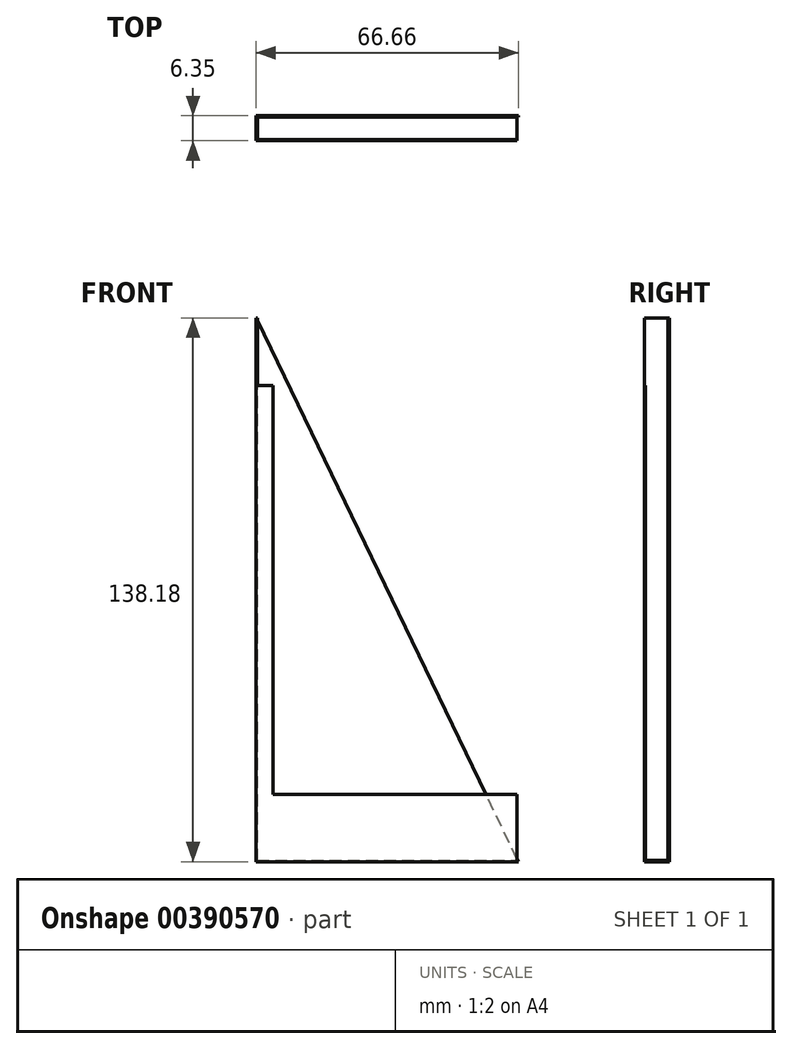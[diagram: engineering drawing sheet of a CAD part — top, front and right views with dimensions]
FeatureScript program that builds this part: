
annotation { "Feature Type Name" : "Feature", "Feature Type Description" : "" }
export const myFeature = defineFeature(function(context is Context, id is Id, definition is map)
    precondition{}
    {
        {
            var Q0;
            Q0=qCreatedBy(makeId("Front.planeOp"),FACE);
            var sketch = newSketch(context, id + "F0", { "sketchPlane" : qUnion([Q0])});
            skLineSegment(sketch, "E0.bottom", {"start": v(-33.53, -69.09) * mm, "end": v(33.13, -69.09) * mm});
            skLineSegment(sketch, "E0.left", {"start": v(-33.53, -69.09) * mm, "end": v(-33.53, 69.09) * mm});
            skLineSegment(sketch, "E1", {"start": v(-29.22, -51.97) * mm, "end": v(-29.22, 60.15) * mm});
            skLineSegment(sketch, "E2", {"start": v(-29.22, -51.97) * mm, "end": v(33.13, -51.97) * mm});
            skLineSegment(sketch, "E3", {"start": v(-29.22, 60.15) * mm, "end": v(-29.22, 69.09) * mm});
            skLineSegment(sketch, "E4", {"start": v(-29.22, 69.09) * mm, "end": v(-33.53, 69.09) * mm});
            skLineSegment(sketch, "E5", {"start": v(33.13, -51.97) * mm, "end": v(33.13, -69.09) * mm});
            skSolve(sketch);
        }
        {
            var Q0;
            Q0 = qSketchRegion(id + "F0", true);
            extrude(context, id + "F1", {"entities" : qUnion([Q0]), "depth" : 6.35 * mm});
        }
        {
            var Q0;
            Q0=qCreatedBy(makeId("Right.planeOp"),FACE);
            var sketch = newSketch(context, id + "F2", { "sketchPlane" : qUnion([Q0])});
            skLineSegment(sketch, "E6.bottom", {"start": v(-6.03, 51.97) * mm, "end": v(-0.32, 51.97) * mm});
            skLineSegment(sketch, "E6.top", {"start": v(-6.03, 68.77) * mm, "end": v(-0.32, 68.77) * mm});
            skLineSegment(sketch, "E6.left", {"start": v(-6.03, 51.97) * mm, "end": v(-6.03, 68.77) * mm});
            skLineSegment(sketch, "E6.right", {"start": v(-0.32, 51.97) * mm, "end": v(-0.32, 68.77) * mm});
            skLineSegment(sketch, "E7.bottom", {"start": v(-0.32, -51.97) * mm, "end": v(-6.03, -51.97) * mm});
            skLineSegment(sketch, "E7.top", {"start": v(-6.03, -68.77) * mm, "end": v(-0.32, -68.77) * mm});
            skLineSegment(sketch, "E7.left", {"start": v(-6.03, -51.97) * mm, "end": v(-6.03, -68.77) * mm});
            skLineSegment(sketch, "E7.right", {"start": v(-0.32, -51.97) * mm, "end": v(-0.32, -68.77) * mm});
            skSolve(sketch);
        }
        {
            var Q0;
            Q0 = qSketchRegion(id + "F2", true);
            extrude(context, id + "F3", {"entities" : qUnion([Q0]), "operationType" : NewBodyOperationType.REMOVE, "endBound" : BoundingType.SYMMETRIC, "oppositeDirection" : true, "depth" : 66.02 * mm});
        }
        {
            var Q0;
            Q0=qCreatedBy(makeId("Top.planeOp"),FACE);
            var sketch = newSketch(context, id + "F4", { "sketchPlane" : qUnion([Q0])});
            skLineSegment(sketch, "E8.bottom", {"start": v(-33.21, -0.32) * mm, "end": v(-29.22, -0.32) * mm});
            skLineSegment(sketch, "E8.top", {"start": v(-33.21, -6.03) * mm, "end": v(-29.22, -6.03) * mm});
            skLineSegment(sketch, "E8.left", {"start": v(-33.21, -6.03) * mm, "end": v(-33.21, -0.32) * mm});
            skLineSegment(sketch, "E8.right", {"start": v(-29.22, -0.32) * mm, "end": v(-29.22, -6.03) * mm});
            skSolve(sketch);
        }
        {
            var Q0;
            Q0 = qSketchRegion(id + "F4", true);
            extrude(context, id + "F5", {"entities" : qUnion([Q0]), "operationType" : NewBodyOperationType.REMOVE, "endBound" : BoundingType.SYMMETRIC, "oppositeDirection" : true, "depth" : 137.54 * mm});
        }
        {
            var Q0;
            {var subQ1=sQuery(id+"F0.wireOp",EDGE,"E1");Q0=makeQuery(id+"F5.boolean.opBoolean","SPLIT",FACE,{"disambiguationData":[TD([makeQuery(id+"F3.boolean.opBoolean","COPY",FACE,{"derivedFrom":makeQuery(id+"F3.opExtrude","SWEPT_FACE",FACE,{"disambiguationData":[OSD([sQuery(id+"F2.wireOp",EDGE,"E6.right")])]})})])],"derivedFrom":makeQuery(id+"F1.opExtrude","SWEPT_FACE",FACE,{"disambiguationData":[OSD([subQ1])]})});}
            var sketch = newSketch(context, id + "F6", { "sketchPlane" : qUnion([Q0])});
            skLineSegment(sketch, "E9.bottom", {"start": v(-0.32, 69.09) * mm, "end": v(0, 69.09) * mm});
            skLineSegment(sketch, "E9.top", {"start": v(-0.32, -69.09) * mm, "end": v(0, -69.09) * mm});
            skLineSegment(sketch, "E9.left", {"start": v(-0.32, 69.09) * mm, "end": v(-0.32, -69.09) * mm});
            skLineSegment(sketch, "E9.right", {"start": v(0, 69.09) * mm, "end": v(0, -69.09) * mm});
            skSolve(sketch);
        }
        {
            var Q0;
            Q0 = qSketchRegion(id + "F6", true);
            extrude(context, id + "F7", {"entities" : qUnion([Q0]), "operationType" : NewBodyOperationType.ADD, "depth" : 63.5 * mm});
        }
        {
            var Q0;
            Q0=makeQuery(id+"F1.opExtrude","SWEPT_FACE",FACE,{"disambiguationData":[OSD([sQuery(id+"F0.wireOp",EDGE,"E5")])]});
            var sketch = newSketch(context, id + "F8", { "sketchPlane" : qUnion([Q0])});
            skLineSegment(sketch, "E10.bottom", {"start": v(-6.03, -68.77) * mm, "end": v(-0.32, -68.77) * mm});
            skLineSegment(sketch, "E10.top", {"start": v(-6.03, -51.97) * mm, "end": v(-0.32, -51.97) * mm});
            skLineSegment(sketch, "E10.left", {"start": v(-6.03, -68.77) * mm, "end": v(-6.03, -51.97) * mm});
            skLineSegment(sketch, "E10.right", {"start": v(-0.32, -68.77) * mm, "end": v(-0.32, -52.37) * mm});
            skLineSegment(sketch, "E11", {"start": v(-0.32, -52.37) * mm, "end": v(-0.32, -51.97) * mm});
            skSolve(sketch);
        }
        {
            var Q0;
            Q0 = qSketchRegion(id + "F8", true);
            extrude(context, id + "F9", {"entities" : qUnion([Q0]), "operationType" : NewBodyOperationType.REMOVE, "oppositeDirection" : true, "depth" : 25.4 * mm});
        }
        {
            var Q0;
            Q0=makeQuery(id+"F5.boolean.opBoolean","COPY",FACE,{"derivedFrom":makeQuery(id+"F5.opExtrude","SWEPT_FACE",FACE,{"disambiguationData":[OSD([sQuery(id+"F4.wireOp",EDGE,"E8.left")])]})});
            var sketch = newSketch(context, id + "F10", { "sketchPlane" : qUnion([Q0])});
            skLineSegment(sketch, "E12.bottom", {"start": v(-0.32, 70.36) * mm, "end": v(-6.35, 70.36) * mm});
            skLineSegment(sketch, "E12.top", {"start": v(-0.32, 51.97) * mm, "end": v(-6.35, 51.97) * mm});
            skLineSegment(sketch, "E12.left", {"start": v(-0.32, 70.36) * mm, "end": v(-0.32, 51.97) * mm});
            skLineSegment(sketch, "E12.right", {"start": v(-6.35, 70.36) * mm, "end": v(-6.35, 51.97) * mm});
            skSolve(sketch);
        }
        {
            var Q0;
            Q0 = qSketchRegion(id + "F10", true);
            extrude(context, id + "F11", {"entities" : qUnion([Q0]), "operationType" : NewBodyOperationType.REMOVE, "endBound" : BoundingType.THROUGH_ALL, "depth" : 25.4 * mm});
        }
        {
            var Q0;
            Q0=makeQuery(id+"F7.boolean.opBoolean","MERGE",FACE,{"derivedFrom":[makeQuery(id+"F1.opExtrude","CAP_FACE",FACE,{"disambiguationData":[OSD([sQuery(id+"F0.wireOp",EDGE,"E0.bottom"),sQuery(id+"F0.wireOp",EDGE,"E0.left"),sQuery(id+"F0.wireOp",EDGE,"E1"),sQuery(id+"F0.wireOp",EDGE,"E2"),sQuery(id+"F0.wireOp",EDGE,"E3"),sQuery(id+"F0.wireOp",EDGE,"E4"),sQuery(id+"F0.wireOp",EDGE,"E5")])],"isStart":true}),makeQuery(id+"F7.opExtrude","SWEPT_FACE",FACE,{"disambiguationData":[OSD([sQuery(id+"F6.wireOp",EDGE,"E9.right")])]})]});
            var sketch = newSketch(context, id + "F12", { "sketchPlane" : qUnion([Q0])});
            skPoint(sketch, "E13.end.orphan", {"position": v(-34.28, -69.09) * mm});
            skLineSegment(sketch, "E14", {"start": v(-34.28, 69.09) * mm, "end": v(-34.28, -69.09) * mm});
            skLineSegment(sketch, "E15", {"start": v(-34.28, 69.09) * mm, "end": v(33.53, 69.09) * mm});
            skLineSegment(sketch, "E16", {"start": v(-34.28, -69.09) * mm, "end": v(-33.13, -69.09) * mm});
            skLineSegment(sketch, "E17", {"start": v(-33.13, -69.09) * mm, "end": v(33.53, 69.09) * mm});
            skSolve(sketch);
        }
        {
            var Q0;
            Q0 = qSketchRegion(id + "F12", true);
            extrude(context, id + "F13", {"entities" : qUnion([Q0]), "operationType" : NewBodyOperationType.REMOVE, "oppositeDirection" : true, "depth" : 0.32 * mm});
        }
        {
            var Q0;
            Q0=makeQuery(id+"F1.opExtrude","CAP_FACE",FACE,{"disambiguationData":[OSD([sQuery(id+"F0.wireOp",EDGE,"E0.bottom"),sQuery(id+"F0.wireOp",EDGE,"E0.left"),sQuery(id+"F0.wireOp",EDGE,"E1"),sQuery(id+"F0.wireOp",EDGE,"E2"),sQuery(id+"F0.wireOp",EDGE,"E3"),sQuery(id+"F0.wireOp",EDGE,"E4"),sQuery(id+"F0.wireOp",EDGE,"E5")])],"isStart":false});
            var sketch = newSketch(context, id + "F14", { "sketchPlane" : qUnion([Q0])});
            skLineSegment(sketch, "E18.bottom", {"start": v(33.13, -69.09) * mm, "end": v(32.81, -69.09) * mm});
            skLineSegment(sketch, "E18.top", {"start": v(33.13, -51.97) * mm, "end": v(32.81, -51.97) * mm});
            skLineSegment(sketch, "E18.left", {"start": v(33.13, -69.09) * mm, "end": v(33.13, -51.97) * mm});
            skLineSegment(sketch, "E18.right", {"start": v(32.81, -69.09) * mm, "end": v(32.81, -51.97) * mm});
            skSolve(sketch);
        }
        {
            var Q0;
            Q0 = qSketchRegion(id + "F14", true);
            var Q1;
            Q1=makeQuery(id+"F11.boolean.opBoolean","MERGE",FACE,{"derivedFrom":[makeQuery(id+"F9.boolean.opBoolean","MERGE",FACE,{"derivedFrom":[makeQuery(id+"F7.boolean.opBoolean","MERGE",FACE,{"derivedFrom":[makeQuery(id+"F5.boolean.opBoolean","MERGE",FACE,{"derivedFrom":[makeQuery(id+"F3.boolean.opBoolean","COPY",FACE,{"derivedFrom":makeQuery(id+"F3.opExtrude","SWEPT_FACE",FACE,{"disambiguationData":[OSD([sQuery(id+"F2.wireOp",EDGE,"E6.right")])]})}),makeQuery(id+"F3.boolean.opBoolean","COPY",FACE,{"derivedFrom":makeQuery(id+"F3.opExtrude","SWEPT_FACE",FACE,{"disambiguationData":[OSD([sQuery(id+"F2.wireOp",EDGE,"E7.right")])]})}),makeQuery(id+"F5.opExtrude","SWEPT_FACE",FACE,{"disambiguationData":[OSD([sQuery(id+"F4.wireOp",EDGE,"E8.bottom")])]})]}),makeQuery(id+"F7.opExtrude","SWEPT_FACE",FACE,{"disambiguationData":[OSD([sQuery(id+"F6.wireOp",EDGE,"E9.left")])]})]}),makeQuery(id+"F9.opExtrude","SWEPT_FACE",FACE,{"disambiguationData":[OSD([sQuery(id+"F8.wireOp",EDGE,"E10.right"),sQuery(id+"F8.wireOp",EDGE,"E11")])]})]}),makeQuery(id+"F11.opExtrude","SWEPT_FACE",FACE,{"disambiguationData":[OSD([sQuery(id+"F10.wireOp",EDGE,"E12.left")])]})]});
            extrude(context, id + "F15", {"entities" : qUnion([Q0]), "operationType" : NewBodyOperationType.REMOVE, "endBound" : BoundingType.UP_TO_SURFACE, "oppositeDirection" : true, "endBoundEntityFace" : qUnion([Q1]), "depth" : 25.4 * mm});
        }
    });
